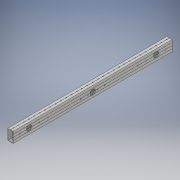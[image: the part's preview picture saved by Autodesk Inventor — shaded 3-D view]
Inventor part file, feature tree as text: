
AUTODESK INVENTOR PART (.ipt)
format: ipt  version: 2017 (Build 210142000, 142)  size: 666,112 bytes
history: native  units: in
note: dims shown in document units (in); Inventor stores cm internally (conversion verified against a paired STEP export)
features: hole x7, reference x4, other x4, extrude x3, sketch x3
ambient origin geometry x8: Origin, YZ Plane, XZ Plane, XY Plane, X Axis, Y Axis, Z Axis, Center Point
bodies: Solid1 (feature_tree)
feature tree (21):
  extrude  "Extrusion1"  Depth=1.0in TaperAngle=0.0deg
  hole  "Hole1"  [1 undecoded]
  hole  "Hole2"  [1 undecoded]
  hole  "Hole3"  [1 undecoded]
  extrude  "Extrusion2"  Depth=1.0in TaperAngle=0.0deg
  extrude  "Extrusion3"  Depth=1.0in
  hole  "Hole4"  [1 undecoded]
  hole  "Hole5"  [1 undecoded]
  hole  "Hole6"  [1 undecoded]
  hole  "Hole7"  [1 undecoded]
  sketch  "Sketch1"  dims[d0=30.0in d1=1.0in d2=0.0in]
  sketch  "Sketch2"  dims[d3=3.0in d4=0.94in d5=1.0in d6=0.75in d7=0.375in d8=0.25in d9=0.5635in d10=1.0in d11=0.8108in d12=0.94in d13=3.0in]
  reference  "Reference1"
  reference  "Reference2"
  reference  "Reference3"
  reference  "Reference4"
  sketch  "Sketch3"  dims[d14=1.0in d15=0.75in d16=0.375in d17=0.25in d18=0.5635in d19=1.0in d20=0.8108in d21=1.0963in d22=15.0in d23=1.0in d24=0.75in d25=0.375in d26=0.25in d27=0.5635in d28=1.0in d29=0.8108in d30=1.0in d31=0.0in d32=1.0in d33=0.0in d34=1.25in d35=1.0in d36=0.19in d37=0.75in d38=0.375in d39=0.25in d40=0.5635in d41=1.0in d42=0.8108in d43=1.0in d44=6.5in d45=0.19in d46=0.75in d47=0.375in d48=0.25in d49=0.5635in d50=1.0in d51=0.8108in d52=1.25in d53=1.0in d54=0.19in d55=0.75in d56=0.375in d57=0.25in d58=0.5635in d59=1.0in d60=0.8108in d61=1.0in d62=6.5in d63=0.19in d64=0.75in d65=0.375in d66=0.25in d67=0.5635in d68=1.0in d69=0.8108in]
  other  "Cut-Extrude2"
  parser-record x1  (decoder bookkeeping rows leaked as tree rows — omitted from the tree; the rows remain in map.json)
  other  "SideFrame.iam"
  other  "WCP_DS_Gearbox:1"
note: 7 required parameter values undecoded (feature->parameter linkage not recoverable at this tier; creation-order binding heuristic only, values carry confidence <= 0.55)
note: 1 file-system path scrubbed to <path> (originals preserved in map.json)
